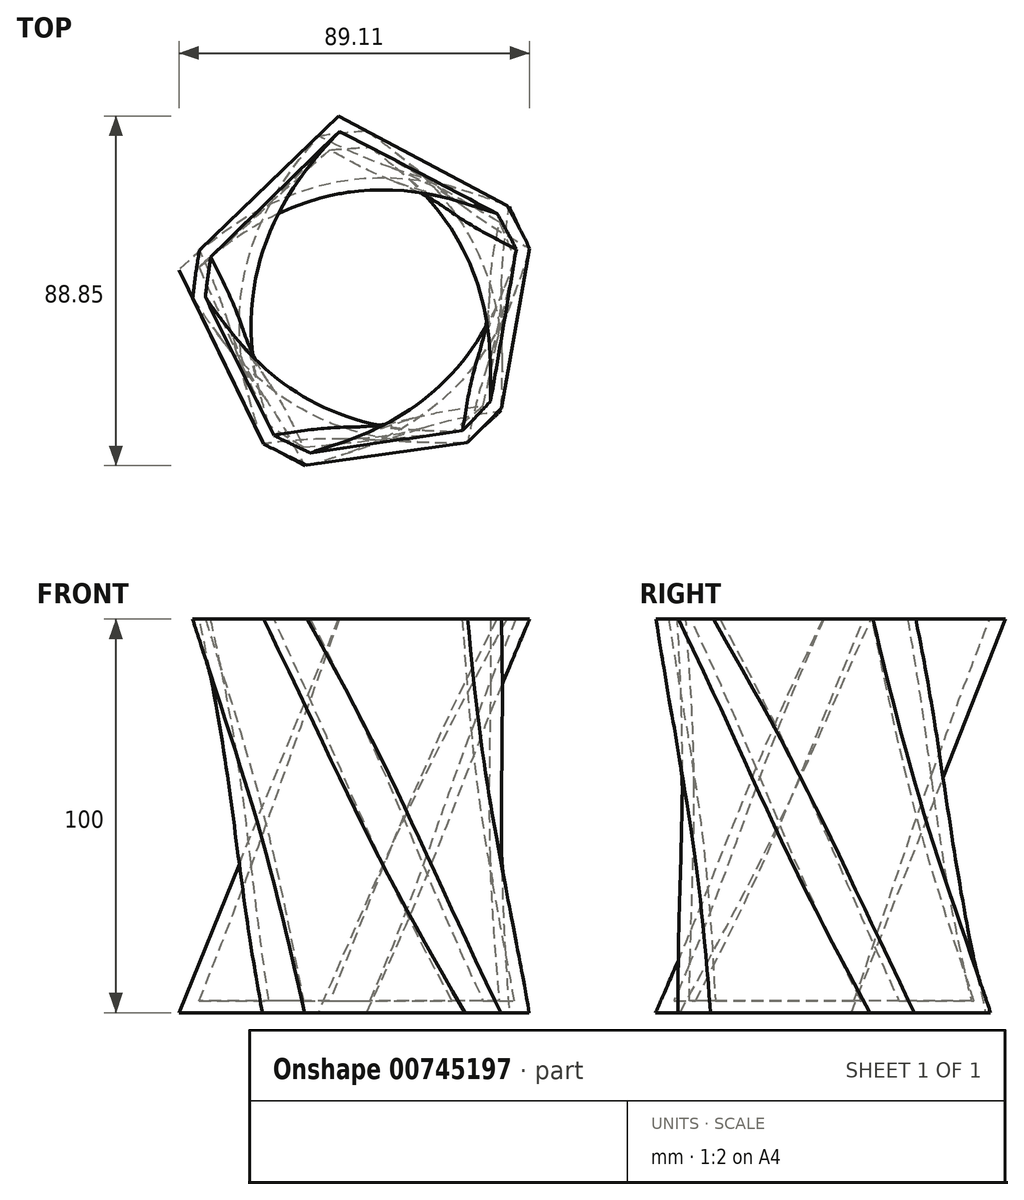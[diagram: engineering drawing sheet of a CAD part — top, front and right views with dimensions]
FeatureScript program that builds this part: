
annotation { "Feature Type Name" : "Feature", "Feature Type Description" : "" }
export const myFeature = defineFeature(function(context is Context, id is Id, definition is map)
    precondition{}
    {
        {
            var Q0;
            Q0=qCreatedBy(makeId("Top.planeOp"),FACE);
            var sketch = newSketch(context, id + "F0", { "sketchPlane" : qUnion([Q0])});
            skCircle(sketch, "E0.cCircle", {"center": v(0, 0) * mm, "radius": 38.81 * mm, "construction": true});
            skLineSegment(sketch, "E0.0", {"start": v(-6.64, 47.51) * mm, "end": v(43.13, 21) * mm});
            skLineSegment(sketch, "E0.1", {"start": v(43.13, 21) * mm, "end": v(33.3, -34.53) * mm});
            skLineSegment(sketch, "E0.2", {"start": v(33.3, -34.53) * mm, "end": v(-22.55, -42.34) * mm});
            skLineSegment(sketch, "E0.3", {"start": v(-22.55, -42.34) * mm, "end": v(-47.24, 8.36) * mm});
            skLineSegment(sketch, "E0.4", {"start": v(-47.24, 8.36) * mm, "end": v(-6.64, 47.51) * mm});
            skPoint(sketch, "E0.0.midPoint", {"position": v(18.24, 34.26) * mm});
            skSolve(sketch);
        }
        {
            var Q0;
            Q0=makeQuery(id+"F0.imprint","IMPRINT",FACE,{"disambiguationData":[TD([[makeQuery(id+"F0.imprint","IMPRINT",EDGE,{"derivedFrom":sQuery(id+"F0.wireOp",EDGE,"E0.0")}),-1.0]])]});
            cPlane(context, id + "F1", {"entities" : qUnion([Q0]), "cplaneType" : CPlaneType.OFFSET, "offset" : 100 * mm, "width" : 150 * mm, "height" : 150 * mm});
        }
        {
            var Q0;
            Q0=qCreatedBy(id+"F1.planeOp",FACE);
            var sketch = newSketch(context, id + "F2", { "sketchPlane" : qUnion([Q0])});
            skLineSegment(sketch, "E1.0", {"start": v(-47.24, 8.36) * mm, "end": v(-6.64, 47.51) * mm});
            skLineSegment(sketch, "E1.1", {"start": v(-6.64, 47.51) * mm, "end": v(43.13, 21) * mm});
            skLineSegment(sketch, "E1.2", {"start": v(-22.55, -42.34) * mm, "end": v(-47.24, 8.36) * mm});
            skLineSegment(sketch, "E1.3", {"start": v(33.3, -34.53) * mm, "end": v(-22.55, -42.34) * mm});
            skLineSegment(sketch, "E1.4", {"start": v(43.13, 21) * mm, "end": v(33.3, -34.53) * mm});
            skSolve(sketch);
        }
        {
            var Q0;
            Q0=makeQuery(id+"F0.imprint","IMPRINT",FACE,{"disambiguationData":[TD([[makeQuery(id+"F0.imprint","IMPRINT",EDGE,{"derivedFrom":sQuery(id+"F0.wireOp",EDGE,"E0.0")}),-1.0]])]});
            var Q1;
            Q1=makeQuery(id+"F2.imprint","IMPRINT",FACE,{"disambiguationData":[TD([[makeQuery(id+"F2.imprint","IMPRINT",EDGE,{"derivedFrom":sQuery(id+"F2.wireOp",EDGE,"E1.0")}),-1.0]])]});
            var Q2;
            Q2=sQuery(id+"F2.wireOp",VERTEX,"E1.2.end");
            var Q3;
            Q3=sQuery(id+"F0.wireOp",VERTEX,"E0.3.start");
            loft(context, id + "F3", {"sheetProfilesArray" : [{ "sheetProfileEntities" : qUnion([Q0]) }, { "sheetProfileEntities" : qUnion([Q1]) }], "matchConnections" : true, "connections" : [{ "connectionEntities" : qUnion([Q2, Q3]), "connectionEdgeQueries" : qUnion([]), "connectionEdgeParameters" : [] }]});
        }
        {
            var Q0;
            Q0=makeQuery(id+"F3.opLoft","SWEPT_EDGE",EDGE,{"disambiguationData":[OSD([sQuery(id+"F0.wireOp",EDGE,"E0.1"),sQuery(id+"F0.wireOp",EDGE,"E0.2"),sQuery(id+"F2.wireOp",EDGE,"E1.2"),sQuery(id+"F2.wireOp",EDGE,"E1.3")])]});
            var Q1;
            Q1=makeQuery(id+"F3.opLoft","SWEPT_EDGE",EDGE,{"disambiguationData":[OSD([sQuery(id+"F0.wireOp",EDGE,"E0.2"),sQuery(id+"F0.wireOp",EDGE,"E0.3"),sQuery(id+"F2.wireOp",EDGE,"E1.0"),sQuery(id+"F2.wireOp",EDGE,"E1.2")])]});
            var Q2;
            Q2=makeQuery(id+"F3.opLoft","SWEPT_EDGE",EDGE,{"disambiguationData":[OSD([sQuery(id+"F0.wireOp",EDGE,"E0.0"),sQuery(id+"F0.wireOp",EDGE,"E0.1"),sQuery(id+"F2.wireOp",EDGE,"E1.3"),sQuery(id+"F2.wireOp",EDGE,"E1.4")])]});
            var Q3;
            Q3=makeQuery(id+"F3.opLoft","SWEPT_EDGE",EDGE,{"disambiguationData":[OSD([sQuery(id+"F0.wireOp",EDGE,"E0.0"),sQuery(id+"F0.wireOp",EDGE,"E0.4"),sQuery(id+"F2.wireOp",EDGE,"E1.1"),sQuery(id+"F2.wireOp",EDGE,"E1.4")])]});
            chamfer(context, id + "F4", {"entities" : qUnion([Q0, Q1, Q2, Q3]), "width" : 10 * mm, "tangentPropagation" : true});
        }
        {
            var Q0;
            Q0=makeQuery(id+"F3.opLoft","CAP_FACE",FACE,{"disambiguationData":[OSD([makeQuery(id+"F2.imprint","IMPRINT",FACE,{"disambiguationData":[TD([[makeQuery(id+"F2.imprint","IMPRINT",EDGE,{"derivedFrom":sQuery(id+"F2.wireOp",EDGE,"E1.0")}),-1.0]])]})])],"isStart":true});
            shell(context, id + "F5", {"entities" : qUnion([Q0]), "thickness" : 3 * mm});
        }
    });
